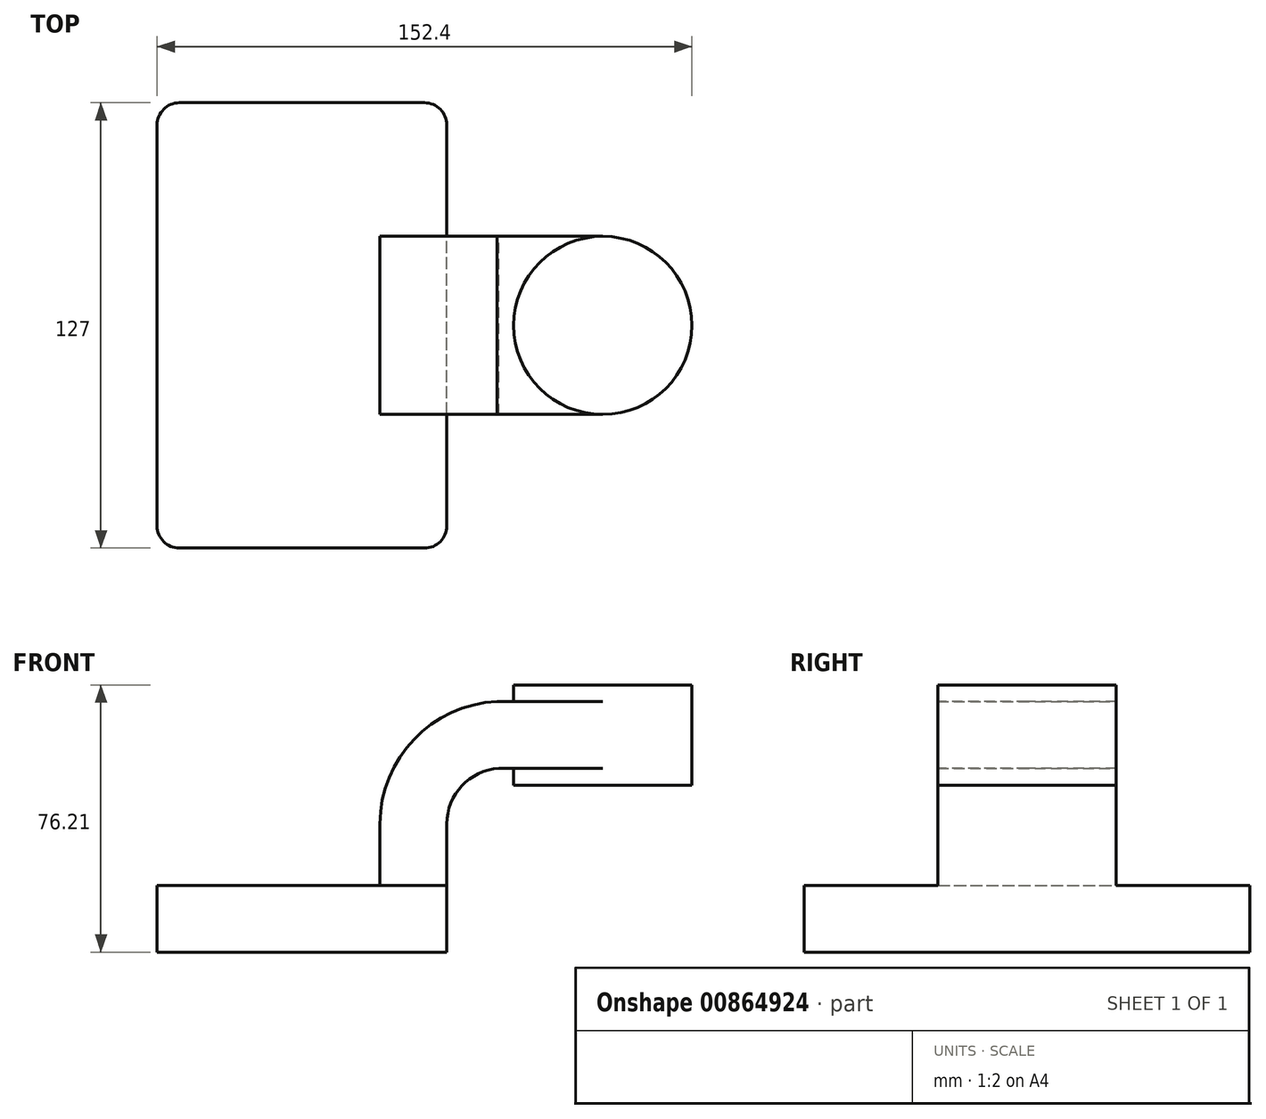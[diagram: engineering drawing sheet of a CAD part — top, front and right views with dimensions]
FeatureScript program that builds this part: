
annotation { "Feature Type Name" : "Feature", "Feature Type Description" : "" }
export const myFeature = defineFeature(function(context is Context, id is Id, definition is map)
    precondition{}
    {
        {
            var Q0;
            Q0=qCreatedBy(makeId("Front.planeOp"),FACE);
            var sketch = newSketch(context, id + "F0", { "sketchPlane" : qUnion([Q0])});
            skLineSegment(sketch, "E0.bottom", {"start": v(-41.27, -9.53) * mm, "end": v(41.28, -9.53) * mm});
            skLineSegment(sketch, "E0.top", {"start": v(-41.28, 9.52) * mm, "end": v(41.28, 9.52) * mm});
            skLineSegment(sketch, "E0.left", {"start": v(-41.28, -9.53) * mm, "end": v(-41.28, 9.52) * mm});
            skLineSegment(sketch, "E0.right", {"start": v(41.28, -9.53) * mm, "end": v(41.28, 9.52) * mm});
            skPoint(sketch, "E0.middle", {"position": v(0, 0) * mm});
            skLineSegment(sketch, "E1.bottom", {"start": v(111.12, 38.1) * mm, "end": v(60.33, 38.1) * mm});
            skLineSegment(sketch, "E1.top", {"start": v(111.12, 66.68) * mm, "end": v(60.33, 66.68) * mm});
            skLineSegment(sketch, "E1.left", {"start": v(111.12, 38.1) * mm, "end": v(111.12, 66.68) * mm});
            skLineSegment(sketch, "E1.right", {"start": v(60.33, 38.1) * mm, "end": v(60.33, 66.68) * mm});
            skPoint(sketch, "E1.middle", {"position": v(85.72, 52.39) * mm});
            skLineSegment(sketch, "E2", {"start": v(41.27, 9.52) * mm, "end": v(41.27, 27.03) * mm});
            skArc(sketch, "E3", {"start": v(41.27, 27.03) * mm, "mid": v(45.56, 37.89) * mm, "end": v(56.12, 42.88) * mm});
            skLineSegment(sketch, "E4", {"start": v(56.12, 42.88) * mm, "end": v(85.72, 42.88) * mm});
            skLineSegment(sketch, "E5.0", {"start": v(55.62, 61.93) * mm, "end": v(85.72, 61.93) * mm});
            skArc(sketch, "E5.1", {"start": v(22.22, 27.03) * mm, "mid": v(31.92, 51.18) * mm, "end": v(55.62, 61.93) * mm});
            skLineSegment(sketch, "E5.2", {"start": v(22.22, 9.52) * mm, "end": v(22.22, 27.03) * mm});
            skLineSegment(sketch, "E6", {"start": v(85.72, 38.1) * mm, "end": v(85.72, 66.68) * mm});
            skFitSpline(sketch, "E7", {"points": [v(-41.27, 9.53) * mm, v(55.62, 61.93) * mm], "startDerivative": vector(0.74, 85.52) * mm, "endDerivative": vector(120.99, 0.38) * mm});
            skSolve(sketch);
        }
        {
            var Q0;
            Q0=makeQuery(id+"F0.imprint","IMPRINT",FACE,{"disambiguationData":[TD([[makeQuery(id+"F0.imprint","IMPRINT",EDGE,{"derivedFrom":sQuery(id+"F0.wireOp",EDGE,"E0.bottom")}),1.0]])]});
            extrude(context, id + "F1", {"entities" : qUnion([Q0]), "endBound" : BoundingType.SYMMETRIC, "depth" : 127 * mm, "offsetDistance" : 25.4 * mm});
        }
        {
            var Q0;
            {var subQ1=sQuery(id+"F0.wireOp",EDGE,"E2");Q0=makeQuery(id+"F0.imprint","IMPRINT",FACE,{"disambiguationData":[TD([[makeQuery(id+"F0.imprint","IMPRINT",EDGE,{"derivedFrom":subQ1}),1.0]])]});}
            var Q1;
            {var subQ0=sQuery(id+"F0.wireOp",EDGE,"E4");var subQ1=sQuery(id+"F0.wireOp",EDGE,"E1.right");var subQ2=makeQuery(id+"F0.imprint","INTERSECT",VERTEX,{"derivedFrom":[subQ1,subQ0]});Q1=makeQuery(id+"F0.imprint","IMPRINT",FACE,{"disambiguationData":[TD([[makeQuery(id+"F0.imprint","IMPRINT",EDGE,{"disambiguationData":[TD([[subQ2,-1.0]])],"derivedFrom":subQ1}),-1.0]])]});}
            extrude(context, id + "F2", {"entities" : qUnion([Q0, Q1]), "operationType" : NewBodyOperationType.ADD, "endBound" : BoundingType.SYMMETRIC, "depth" : 50.8 * mm, "offsetDistance" : 25.4 * mm});
        }
        {
            var Q0;
            Q0=makeQuery(id+"F0.imprint","IMPRINT",FACE,{"disambiguationData":[TD([[makeQuery(id+"F0.imprint","IMPRINT",EDGE,{"derivedFrom":sQuery(id+"F0.wireOp",EDGE,"E5.1")}),1.0]])]});
            extrude(context, id + "F3", {"entities" : qUnion([Q0]), "operationType" : NewBodyOperationType.ADD, "endBound" : BoundingType.SYMMETRIC, "depth" : 15.88 * mm, "offsetDistance" : 25.4 * mm});
        }
        {
            var Q0;
            {var subQ4=sQuery(id+"F0.wireOp",EDGE,"E1.left");Q0=makeQuery(id+"F0.imprint","IMPRINT",FACE,{"disambiguationData":[TD([[makeQuery(id+"F0.imprint","IMPRINT",EDGE,{"derivedFrom":subQ4}),1.0]])]});}
            var Q1;
            Q1=sQuery(id+"F0.wireOp",EDGE,"E6");
            revolve(context, id + "F4", {"operationType" : NewBodyOperationType.ADD, "surfaceOperationType" : NewSurfaceOperationType.NEW, "entities" : qUnion([Q0]), "axis" : qUnion([Q1]), "revolveType" : RevolveType.FULL});
        }
        {
            var Q0;
            Q0=makeQuery(id+"F1.opExtrude","CAP_EDGE",EDGE,{"disambiguationData":[OSD([sQuery(id+"F0.wireOp",EDGE,"E0.left")])],"isStart":false});
            var Q1;
            Q1=makeQuery(id+"F1.opExtrude","CAP_EDGE",EDGE,{"disambiguationData":[OSD([sQuery(id+"F0.wireOp",EDGE,"E0.right")])],"isStart":false});
            var Q2;
            Q2=makeQuery(id+"F1.opExtrude","CAP_EDGE",EDGE,{"disambiguationData":[OSD([sQuery(id+"F0.wireOp",EDGE,"E0.right")])],"isStart":true});
            var Q3;
            Q3=makeQuery(id+"F1.opExtrude","CAP_EDGE",EDGE,{"disambiguationData":[OSD([sQuery(id+"F0.wireOp",EDGE,"E0.left")])],"isStart":true});
            fillet(context, id + "F5", {"entities" : qUnion([Q0, Q1, Q2, Q3]), "radius" : 6.35 * mm, "tangentPropagation" : true, "allowEdgeOverflow" : false});
        }
    });
